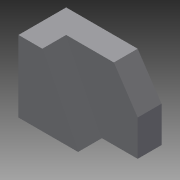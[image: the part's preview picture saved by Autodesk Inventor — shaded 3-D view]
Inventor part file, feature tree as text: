
AUTODESK INVENTOR PART (.ipt)
format: ipt  version: 2015 (Build 190159000, 159)  size: 85,504 bytes
history: native  units: in
note: dims shown in document units (in); Inventor stores cm internally (conversion verified against a paired STEP export)
features: extrude x3, sketch x3
ambient origin geometry x8: Origin, YZ Plane, XZ Plane, XY Plane, X Axis, Y Axis, Z Axis, Center Point
bodies: Solid1 (feature_tree)
feature tree (6):
  extrude  "Extrusion1"  Depth=1.5in
  extrude  "Extrusion2"  Depth=1.0in TaperAngle=0.0deg
  extrude  "Extrusion3"  Depth=0.5in TaperAngle=0.0deg
  sketch  "Sketch1"  dims[d0=2.0in d1=1.5in]
  sketch  "Sketch2"  dims[d2=0.5in d4=1.0in d5=0.0in]
  sketch  "Sketch3"  dims[d8=0.5in d9=0.0in d12=0.5in d13=0.0in]
